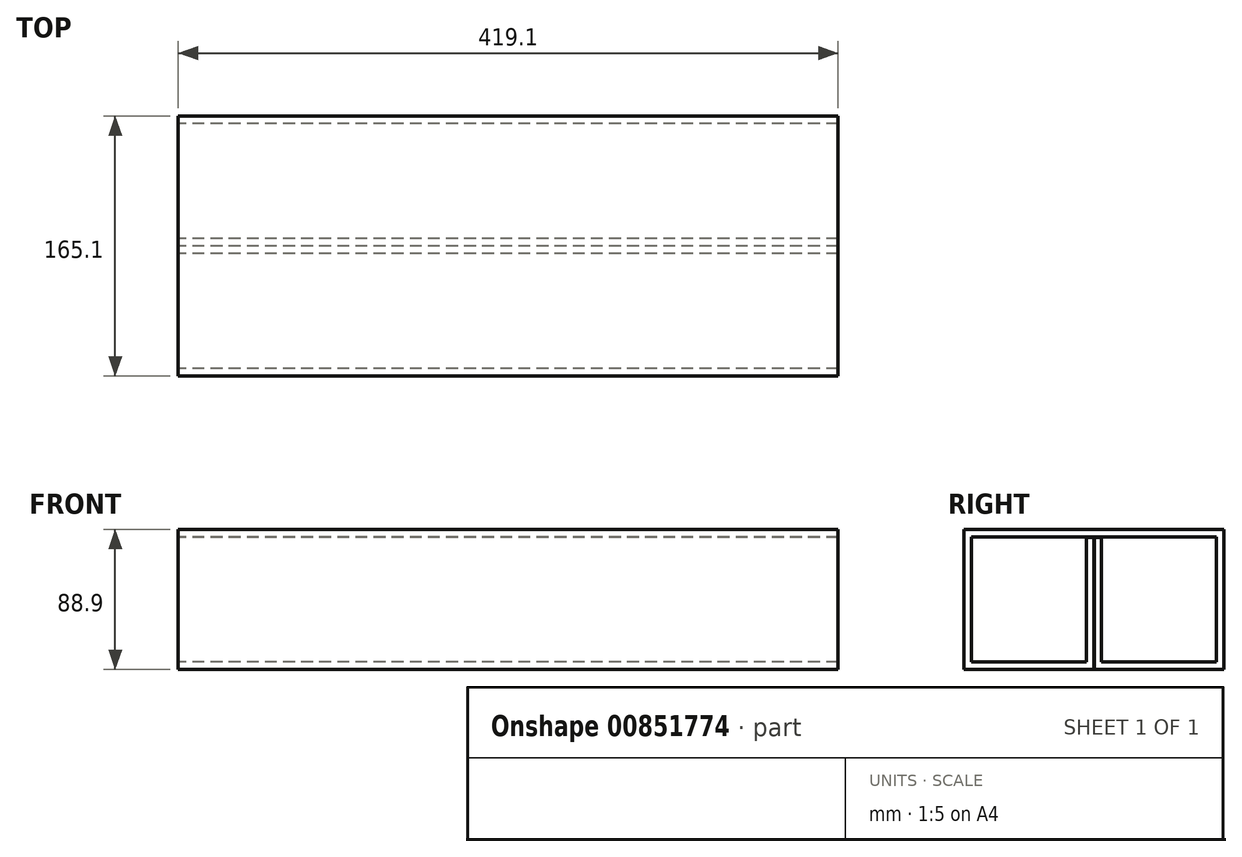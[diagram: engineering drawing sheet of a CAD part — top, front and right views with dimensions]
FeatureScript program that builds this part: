
annotation { "Feature Type Name" : "Feature", "Feature Type Description" : "" }
export const myFeature = defineFeature(function(context is Context, id is Id, definition is map)
    precondition{}
    {
        {
            var Q0;
            Q0=qCreatedBy(makeId("Right.planeOp"),FACE);
            var sketch = newSketch(context, id + "F0", { "sketchPlane" : qUnion([Q0])});
            skLineSegment(sketch, "E0", {"start": v(0, 0) * mm, "end": v(0, 126.35) * mm, "construction": true});
            skLineSegment(sketch, "E1.bottom", {"start": v(-82.55, 88.9) * mm, "end": v(82.55, 88.9) * mm});
            skLineSegment(sketch, "E1.top", {"start": v(-82.55, 0) * mm, "end": v(-0.13, 0) * mm});
            skLineSegment(sketch, "E1.left", {"start": v(-82.55, 88.9) * mm, "end": v(-82.55, 0) * mm});
            skLineSegment(sketch, "E2.0", {"start": v(-77.79, 84.14) * mm, "end": v(77.79, 84.14) * mm});
            skLineSegment(sketch, "E2.1", {"start": v(-77.79, 84.14) * mm, "end": v(-77.79, 4.76) * mm});
            skLineSegment(sketch, "E2.2", {"start": v(-77.79, 4.76) * mm, "end": v(-4.76, 4.76) * mm});
            skLineSegment(sketch, "E2.3", {"start": v(-4.76, 83.88) * mm, "end": v(-4.76, 4.76) * mm});
            skLineSegment(sketch, "E3.MirrorCS", {"start": v(82.55, 88.9) * mm, "end": v(82.55, 0) * mm});
            skLineSegment(sketch, "E4.MirrorCS", {"start": v(4.76, 83.88) * mm, "end": v(4.76, 4.76) * mm});
            skLineSegment(sketch, "E5.MirrorCS", {"start": v(77.79, 4.76) * mm, "end": v(4.76, 4.76) * mm});
            skLineSegment(sketch, "E6.MirrorCS", {"start": v(77.79, 84.14) * mm, "end": v(77.79, 4.76) * mm});
            skLineSegment(sketch, "E7.left", {"start": v(-0.13, 0) * mm, "end": v(-0.13, 83.88) * mm});
            skLineSegment(sketch, "E7.right", {"start": v(0.13, 0) * mm, "end": v(0.13, 83.88) * mm});
            skLineSegment(sketch, "E8.trimOffspring", {"start": v(0.13, 0) * mm, "end": v(82.55, 0) * mm});
            skLineSegment(sketch, "E9", {"start": v(-4.76, 83.88) * mm, "end": v(-0.13, 83.88) * mm});
            skPoint(sketch, "E10.orphan", {"position": v(4.76, 84.14) * mm});
            skLineSegment(sketch, "E11.trimOffspring", {"start": v(0.13, 83.88) * mm, "end": v(4.76, 83.88) * mm});
            skPoint(sketch, "E12.orphan", {"position": v(-4.76, 84.14) * mm});
            skSolve(sketch);
        }
        {
            var Q0;
            Q0=qSketchRegion(id+"F0",true);
            extrude(context, id + "F1", {"entities" : qUnion([Q0]), "endBound" : BoundingType.SYMMETRIC, "depth" : 419.1 * mm, "offsetDistance" : 25.4 * mm});
        }
    });
